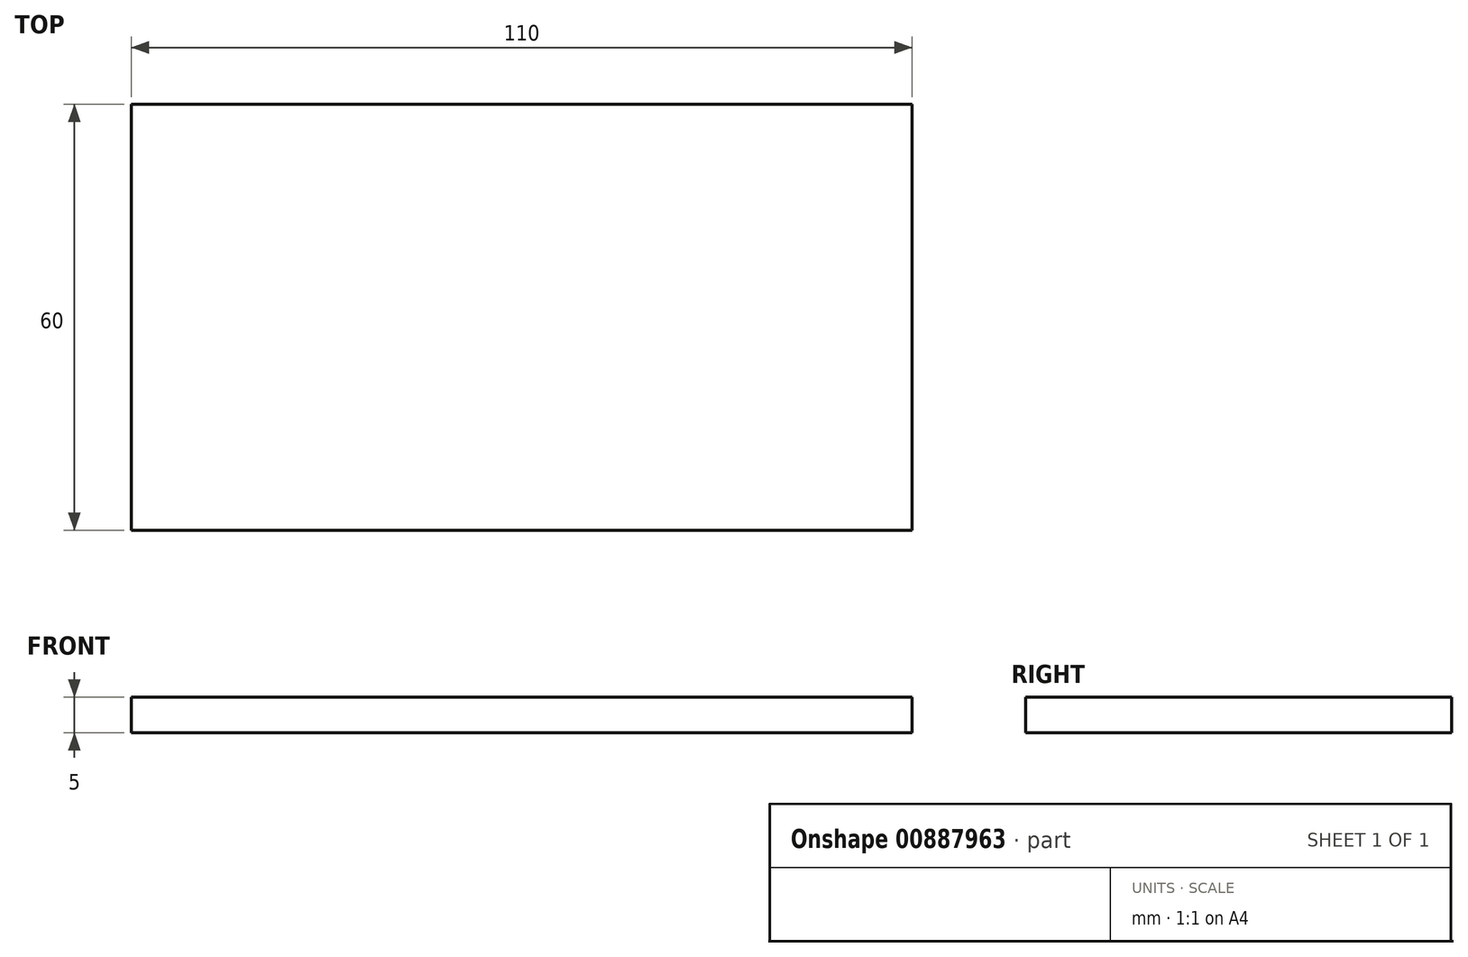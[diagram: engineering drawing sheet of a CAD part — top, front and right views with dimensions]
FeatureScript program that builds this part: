
annotation { "Feature Type Name" : "Feature", "Feature Type Description" : "" }
export const myFeature = defineFeature(function(context is Context, id is Id, definition is map)
    precondition{}
    {
        {
            var Q0;
            Q0=qCreatedBy(makeId("Top.planeOp"),FACE);
            var sketch = newSketch(context, id + "F0", { "sketchPlane" : qUnion([Q0])});
            skLineSegment(sketch, "E0.bottom", {"start": v(-58.6, 26.06) * mm, "end": v(51.4, 26.06) * mm});
            skLineSegment(sketch, "E0.top", {"start": v(-58.6, -33.94) * mm, "end": v(51.4, -33.94) * mm});
            skLineSegment(sketch, "E0.left", {"start": v(-58.6, 26.06) * mm, "end": v(-58.6, -33.94) * mm});
            skLineSegment(sketch, "E0.right", {"start": v(51.4, 26.06) * mm, "end": v(51.4, -33.94) * mm});
            skSolve(sketch);
        }
        {
            var Q0;
            Q0 = qSketchRegion(id + "F0", true);
            extrude(context, id + "F1", {"entities" : qUnion([Q0]), "depth" : 5 * mm, "offsetDistance" : 25 * mm});
        }
    });
